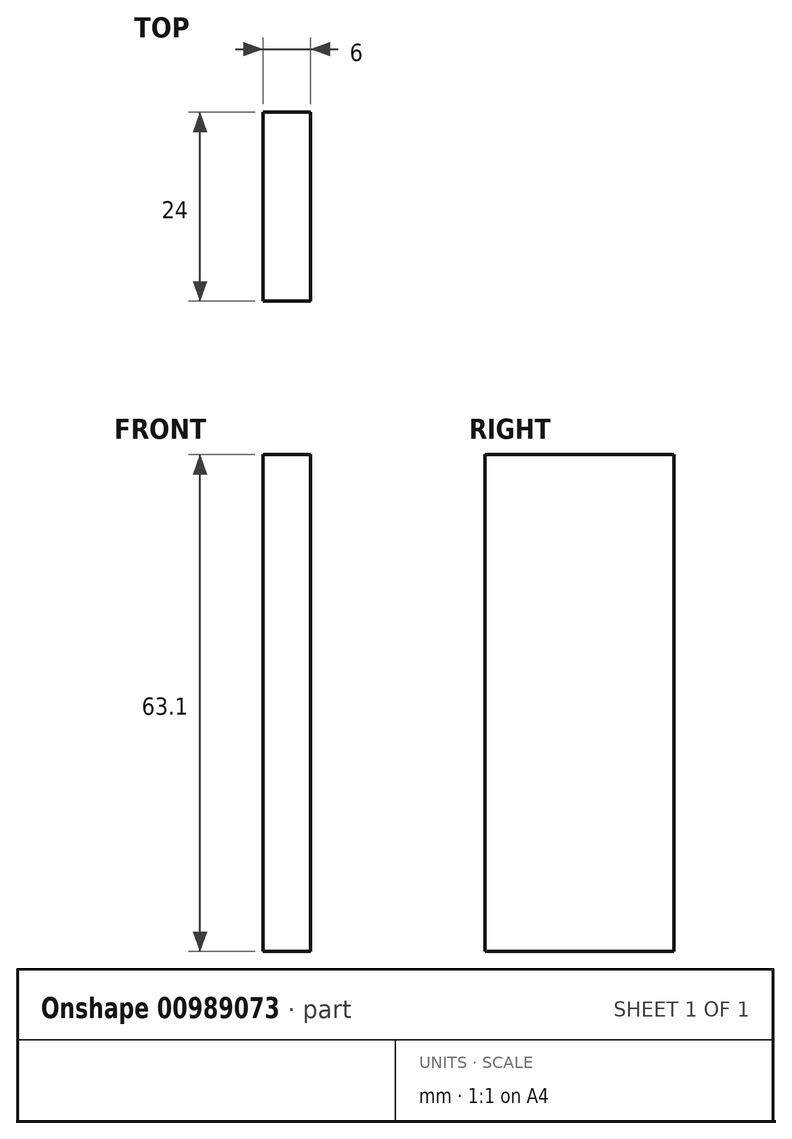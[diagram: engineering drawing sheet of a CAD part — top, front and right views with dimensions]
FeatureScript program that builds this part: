
annotation { "Feature Type Name" : "Feature", "Feature Type Description" : "" }
export const myFeature = defineFeature(function(context is Context, id is Id, definition is map)
    precondition{}
    {
        {
            var Q0;
            Q0=qCreatedBy(makeId("Front.planeOp"),FACE);
            var sketch = newSketch(context, id + "F0", { "sketchPlane" : qUnion([Q0])});
            skLineSegment(sketch, "E0.bottom", {"start": v(0, 0) * mm, "end": v(-6, 0) * mm});
            skLineSegment(sketch, "E0.top", {"start": v(0, 63.1) * mm, "end": v(-6, 63.1) * mm});
            skLineSegment(sketch, "E0.left", {"start": v(0, 0) * mm, "end": v(0, 63.1) * mm});
            skLineSegment(sketch, "E0.right", {"start": v(-6, 0) * mm, "end": v(-6, 63.1) * mm});
            skSolve(sketch);
        }
        {
            var Q0;
            Q0=makeQuery(id+"F0.imprint","IMPRINT",FACE,{"disambiguationData":[TD([[makeQuery(id+"F0.imprint","IMPRINT",EDGE,{"derivedFrom":sQuery(id+"F0.wireOp",EDGE,"E0.bottom")}),-1.0]])]});
            extrude(context, id + "F1", {"entities" : qUnion([Q0]), "depth" : (30 - 6) * mm, "offsetDistance" : 25 * mm});
        }
    });
